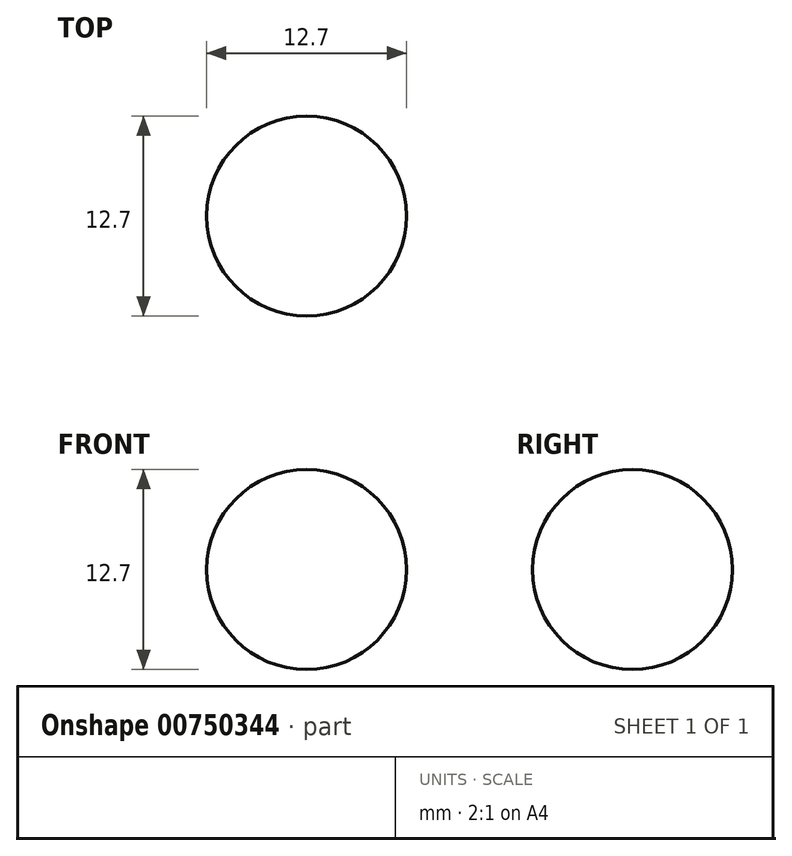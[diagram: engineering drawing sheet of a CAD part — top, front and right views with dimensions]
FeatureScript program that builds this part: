
annotation { "Feature Type Name" : "Feature", "Feature Type Description" : "" }
export const myFeature = defineFeature(function(context is Context, id is Id, definition is map)
    precondition{}
    {
        {
            var Q0;
            Q0=qCreatedBy(makeId("Front.planeOp"),FACE);
            var sketch = newSketch(context, id + "F0", { "sketchPlane" : qUnion([Q0])});
            skCircle(sketch, "E0", {"center": v(-13.99, 17.3) * mm, "radius": 6.35 * mm});
            skLineSegment(sketch, "E1", {"start": v(-13.99, 23.65) * mm, "end": v(-13.99, 10.95) * mm});
            skSolve(sketch);
        }
        {
            var Q0;
            {var subQ0=sQuery(id+"F0.wireOp",EDGE,"E1");Q0=makeQuery(id+"F0.imprint","IMPRINT",FACE,{"disambiguationData":[TD([[makeQuery(id+"F0.imprint","IMPRINT",EDGE,{"derivedFrom":subQ0}),1.0]])]});}
            var Q1;
            Q1=sQuery(id+"F0.wireOp",EDGE,"E1");
            revolve(context, id + "F1", {"surfaceOperationType" : NewSurfaceOperationType.NEW, "entities" : qUnion([Q0]), "axis" : qUnion([Q1]), "revolveType" : RevolveType.FULL});
        }
    });
